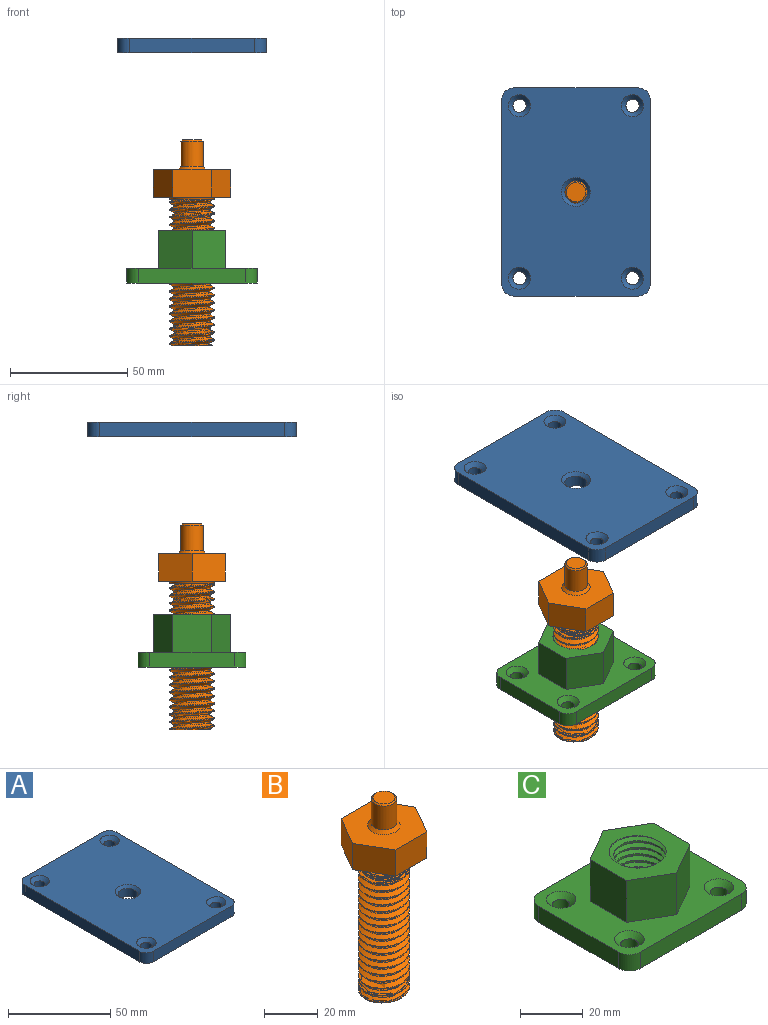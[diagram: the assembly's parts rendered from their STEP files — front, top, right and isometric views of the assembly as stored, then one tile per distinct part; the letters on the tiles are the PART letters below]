
ASSEMBLY  parts=3 mates=2
PART A: 20 faces, bbox 63.5x88.9x6.4 mm
  f0: plane 78.74x6.35mm, normal (-1,0,0), area 500mm2, adj f9,f10,f11,f14
  f1: plane 53.34x6.35mm, normal (0,-1,0), area 338.7mm2, adj f9,f10,f11,f12
  f2: plane 78.74x6.35mm, normal (1,0,0), area 500mm2, adj f9,f10,f12,f13
  f3: cylinder r=4.76mm len=9.53mm, axis (0,0,-1), area 148.2mm2, adj f10,f19
  f4: cylinder r=2.81mm len=5.61mm, axis (0,0,-1), area 78.4mm2, adj f10,f15
  f5: cylinder r=2.81mm len=5.61mm, axis (0,0,-1), area 78.4mm2, adj f10,f16
  f6: cylinder r=2.81mm len=5.61mm, axis (0,0,-1), area 78.4mm2, adj f10,f17
  f7: plane 53.34x6.35mm, normal (0,1,0), area 338.7mm2, adj f9,f10,f13,f14
  f8: cylinder r=2.81mm len=5.61mm, axis (0,0,-1), area 78.4mm2, adj f10,f18
  f9: plane 88.9x63.5mm, normal (0,0,1), area 5224.8mm2, adj f0,f1,f2,f7,f11,f12,f13,f14
  f10: plane 88.9x63.5mm, normal (0,0,-1), area 5452.7mm2, adj f0,f1,f2,f3,f4,f5,f6,f7
  f11: cylinder r=5.08mm len=6.35mm, axis (0,0,1), area 50.7mm2, adj f0,f1,f9,f10
  f12: cylinder r=5.08mm len=6.35mm, axis (0,0,-1), area 50.7mm2, adj f1,f2,f9,f10
  f13: cylinder r=5.08mm len=6.35mm, axis (0,0,1), area 50.7mm2, adj f2,f7,f9,f10
  f14: cylinder r=5.08mm len=6.35mm, axis (0,0,-1), area 50.7mm2, adj f0,f7,f9,f10
  f15: cone r=2.81mm half-angle=45deg, axis (0,0,1), area 63.6mm2, adj f4,f9
  f16: cone r=4.71mm half-angle=45deg, axis (0,0,1), area 63.6mm2, adj f5,f9
  f17: cone r=2.81mm half-angle=45deg, axis (0,0,1), area 63.6mm2, adj f6,f9
  f18: cone r=4.71mm half-angle=45deg, axis (0,0,1), area 63.6mm2, adj f8,f9
  f19: cone r=4.76mm half-angle=45deg, axis (0,0,1), area 67.8mm2, adj f3,f9
PART B: 19 faces, bbox 33.9x29.5x90.4 mm
  f0: plane 14.29x11.91mm, normal (0.87,0.5,0), area 196.4mm2, adj f1,f5,f6,f7
  f1: plane 16.5x11.91mm, normal (0,1,0), area 196.4mm2, adj f0,f2,f6,f7
  f2: plane 14.29x11.91mm, normal (-0.87,0.5,0), area 196.4mm2, adj f1,f3,f6,f7
  f3: plane 14.29x11.91mm, normal (-0.87,-0.5,0), area 196.4mm2, adj f2,f4,f6,f7
  f4: plane 16.5x11.91mm, normal (0,-1,0), area 196.4mm2, adj f3,f5,f6,f7
  f5: plane 14.29x11.91mm, normal (0.87,-0.5,0), area 196.4mm2, adj f0,f4,f6,f7
  f6: plane 33x28.58mm, normal (0,0,1), area 592.8mm2, adj f0,f1,f2,f3,f4,f5,f18
  f7: plane 33x28.58mm, normal (0,0,-1), area 374.7mm2, adj f0,f1,f2,f3,f4,f5,f10
  f8: cylinder r=9.53mm len=62.74mm, axis (0,0,1), area 1796.1mm2, adj f9,f10,f12,f13
  f9: plane 18.11x17.98mm, normal (0,0,-1), area 230mm2, adj f8,f11,f12,f13
  f10: torus R=10.29mm, axis (0,0,1), area 73.7mm2, adj f7,f8,f14
  f11: bspline ~64.82x18.03mm, area 843.3mm2, adj f9,f12,f13,f14
  f12: bspline ~65.55x22mm, area 2114.7mm2, adj f8,f9,f11,f14
  f13: bspline ~65.02x22mm, area 2152.2mm2, adj f8,f9,f11,f14
  f14: plane 19.93x19.93mm, normal (0,0,-1), area 55mm2, adj f10,f11,f12,f13
  f15: cylinder r=4.76mm len=10.8mm, axis (0,0,-1), area 323mm2, adj f17,f18
  f16: plane 8.26x8.26mm, normal (0,0,1), area 53.5mm2, adj f17
  f17: cone r=4.13mm half-angle=45deg, axis (0,0,-1), area 25.1mm2, adj f15,f16
  f18: cone r=4.76mm half-angle=45deg, axis (0,0,-1), area 60.9mm2, adj f6,f15
PART C: 29 faces, bbox 56.3x46.8x25.4 mm
  f0: plane 33.76x29.34mm, normal (0,0,1), area 452.3mm2, adj f15,f16,f17,f18,f19,f20,f21,f22
  f1: plane 55.56x46.04mm, normal (0,0,1), area 1549.7mm2, adj f2,f3,f4,f8,f11,f12,f13,f14
  f2: plane 35.88x6.35mm, normal (-1,0,0), area 227.8mm2, adj f1,f10,f11,f14
  f3: plane 45.4x6.35mm, normal (0,1,0), area 288.3mm2, adj f1,f10,f11,f12
  f4: plane 35.88x6.35mm, normal (1,0,0), area 227.8mm2, adj f1,f10,f12,f13
  f5: cylinder r=2.81mm len=5.61mm, axis (0,0,1), area 78.4mm2, adj f10,f28
  f6: cylinder r=2.81mm len=5.61mm, axis (0,0,1), area 78.4mm2, adj f10,f27
  f7: cylinder r=2.81mm len=5.61mm, axis (0,0,1), area 78.4mm2, adj f10,f26
  f8: plane 45.4x6.35mm, normal (0,-1,0), area 288.3mm2, adj f1,f10,f13,f14
  f9: cylinder r=2.81mm len=5.61mm, axis (0,0,1), area 78.4mm2, adj f10,f25
  f10: plane 56.3x46.78mm, normal (0,0,-1), area 2182mm2, adj f2,f3,f4,f5,f6,f7,f8,f9
  f11: cylinder r=5.08mm len=6.35mm, axis (0,0,-1), area 50.7mm2, adj f1,f2,f3,f10
  f12: cylinder r=5.08mm len=6.35mm, axis (0,0,1), area 50.7mm2, adj f1,f3,f4,f10
  f13: cylinder r=5.08mm len=6.35mm, axis (0,0,-1), area 50.7mm2, adj f1,f4,f8,f10
  f14: cylinder r=5.08mm len=6.35mm, axis (0,0,1), area 50.7mm2, adj f1,f2,f8,f10
  f15: plane 16.27x14.29mm, normal (-0.5,0.87,0), area 268.4mm2, adj f0,f1,f16,f20
  f16: plane 16.5x16.27mm, normal (-1,0,0), area 268.4mm2, adj f0,f1,f15,f17
  f17: plane 16.27x14.29mm, normal (-0.5,-0.87,0), area 268.4mm2, adj f0,f1,f16,f18
  f18: plane 16.27x14.29mm, normal (0.5,-0.87,0), area 268.4mm2, adj f0,f1,f17,f19
  f19: plane 16.5x16.27mm, normal (1,0,0), area 268.4mm2, adj f0,f1,f18,f20
  f20: plane 16.27x14.29mm, normal (0.5,0.87,0), area 268.4mm2, adj f0,f1,f15,f19
  f21: bspline ~24.5x22.53mm, area 806.2mm2, adj f0,f10,f23,f24
  f22: bspline ~24.5x22.53mm, area 808.4mm2, adj f0,f10,f23,f24
  f23: bspline ~23.6x22.8mm, area 202.5mm2, adj f0,f10,f21,f22
  f24: cylinder r=8.38mm len=22.62mm, axis (0,0,-1), area 372mm2, adj f0,f10,f21,f22
  f25: cone r=2.81mm half-angle=45deg, axis (0,0,1), area 63.6mm2, adj f1,f9
  f26: cone r=4.71mm half-angle=45deg, axis (0,0,1), area 63.6mm2, adj f1,f7
  f27: cone r=2.81mm half-angle=45deg, axis (0,0,1), area 63.6mm2, adj f1,f6
  f28: cone r=4.71mm half-angle=45deg, axis (0,0,1), area 63.6mm2, adj f1,f5
PLACE A t=(16.95,11.84,18.49)mm
PLACE B t=(16.95,11.84,-43.19)mm
PLACE C t=(72.52,11.84,-86.16)mm fixed
MATE slider B.f15 <-> A.f3  axis (0,0,-1) through (16.95,11.84,-24.62)mm
MATE slider C.f24 <-> B.f15  axis (0,0,1) through (16.95,11.84,-57.19)mm
